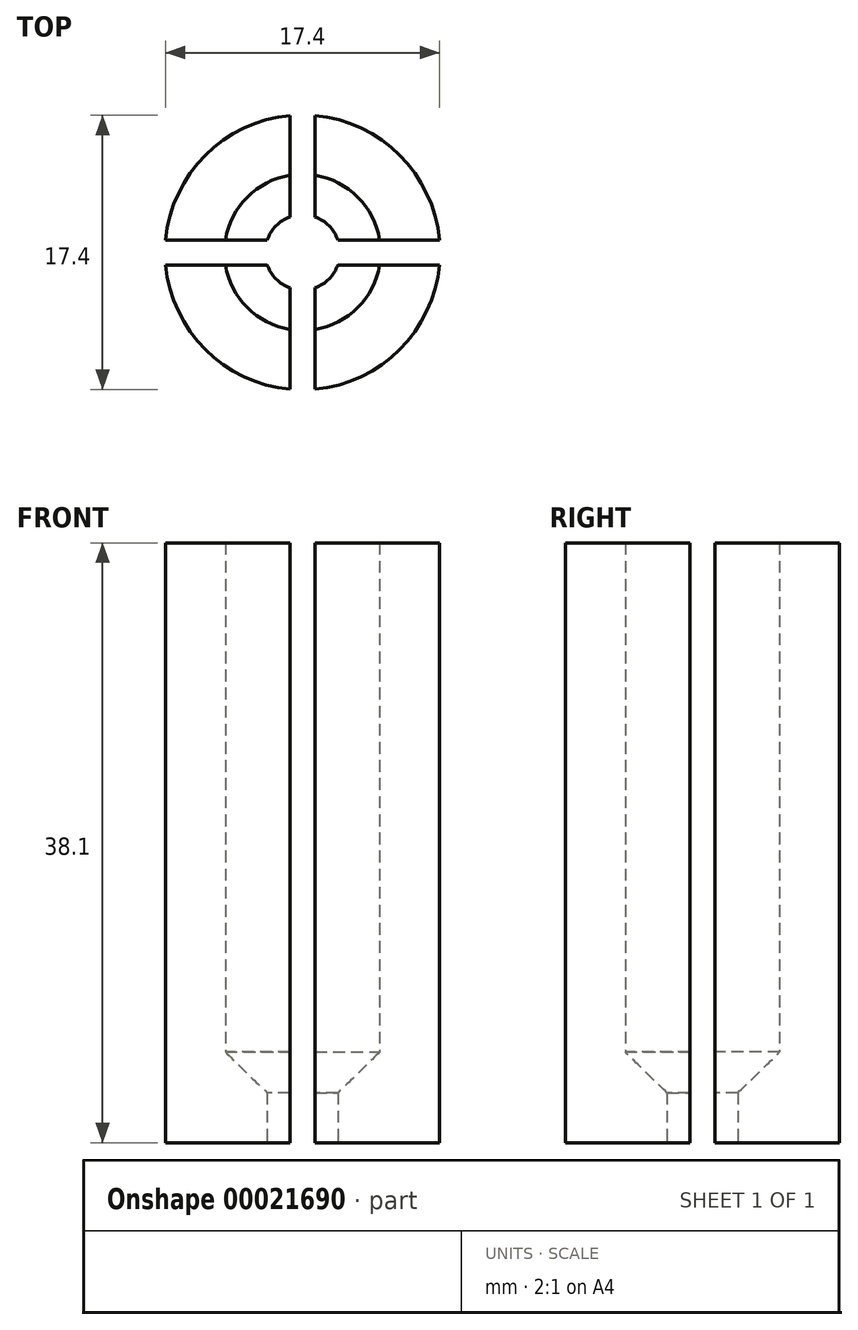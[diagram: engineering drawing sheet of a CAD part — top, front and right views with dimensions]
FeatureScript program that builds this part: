
annotation { "Feature Type Name" : "Feature", "Feature Type Description" : "" }
export const myFeature = defineFeature(function(context is Context, id is Id, definition is map)
    precondition{}
    {
        {
            var Q0;
            Q0=qCreatedBy(makeId("Front.planeOp"),FACE);
            var sketch = newSketch(context, id + "F0", { "sketchPlane" : qUnion([Q0])});
            skLineSegment(sketch, "E0", {"start": v(-16.12, 0) * mm, "end": v(18.02, 0) * mm, "construction": true});
            skLineSegment(sketch, "E1", {"start": v(-8.73, 0) * mm, "end": v(-2.38, 0) * mm});
            skLineSegment(sketch, "E2", {"start": v(-2.38, 0) * mm, "end": v(-2.38, 3.18) * mm});
            skLineSegment(sketch, "E3", {"start": v(-2.38, 3.18) * mm, "end": v(-4.96, 5.75) * mm});
            skLineSegment(sketch, "E4", {"start": v(-4.96, 5.75) * mm, "end": v(-4.96, 38.1) * mm});
            skLineSegment(sketch, "E5", {"start": v(-4.96, 38.1) * mm, "end": v(-8.73, 38.1) * mm});
            skLineSegment(sketch, "E6", {"start": v(-8.73, 38.1) * mm, "end": v(-8.73, 0) * mm});
            skLineSegment(sketch, "E7", {"start": v(0, -2.72) * mm, "end": v(0, 42.46) * mm, "construction": true});
            skSolve(sketch);
        }
        {
            var Q0;
            Q0=makeQuery(id+"F0.imprint","IMPRINT",FACE,{"disambiguationData":[TD([[makeQuery(id+"F0.imprint","IMPRINT",EDGE,{"derivedFrom":sQuery(id+"F0.wireOp",EDGE,"E1")}),1.0]])]});
            var Q1;
            Q1=sQuery(id+"F0.wireOp",EDGE,"E7");
            revolve(context, id + "F1", {"entities" : qUnion([Q0]), "axis" : qUnion([Q1]), "revolveType" : RevolveType.FULL});
        }
        {
            var Q0;
            Q0=makeQuery(id+"F1.opRevolve","SWEPT_FACE",FACE,{"disambiguationData":[OSD([sQuery(id+"F0.wireOp",EDGE,"E5")])]});
            var sketch = newSketch(context, id + "F2", { "sketchPlane" : qUnion([Q0])});
            skLineSegment(sketch, "E8", {"start": v(-0.8, 8.73) * mm, "end": v(0.8, 8.73) * mm});
            skLineSegment(sketch, "E9", {"start": v(0.8, 8.73) * mm, "end": v(0.8, 0.8) * mm});
            skLineSegment(sketch, "E10", {"start": v(0.8, 0.8) * mm, "end": v(8.73, 0.8) * mm});
            skLineSegment(sketch, "E11", {"start": v(8.73, 0.8) * mm, "end": v(8.73, -0.8) * mm});
            skLineSegment(sketch, "E12", {"start": v(8.73, -0.8) * mm, "end": v(0.8, -0.8) * mm});
            skLineSegment(sketch, "E13", {"start": v(0.8, -0.8) * mm, "end": v(0.8, -8.73) * mm});
            skLineSegment(sketch, "E14", {"start": v(0.8, -8.73) * mm, "end": v(-0.8, -8.73) * mm});
            skLineSegment(sketch, "E15", {"start": v(-0.8, -8.73) * mm, "end": v(-0.8, -0.8) * mm});
            skLineSegment(sketch, "E16", {"start": v(-0.8, -0.8) * mm, "end": v(-8.73, -0.8) * mm});
            skLineSegment(sketch, "E17", {"start": v(-8.73, -0.8) * mm, "end": v(-8.73, 0.8) * mm});
            skLineSegment(sketch, "E18", {"start": v(-8.73, 0.8) * mm, "end": v(-0.8, 0.8) * mm});
            skLineSegment(sketch, "E19", {"start": v(-0.8, 0.8) * mm, "end": v(-0.8, 8.73) * mm});
            skLineSegment(sketch, "E20", {"start": v(13.68, 0) * mm, "end": v(-10.76, 0) * mm, "construction": true});
            skLineSegment(sketch, "E21", {"start": v(0, -10.25) * mm, "end": v(0, 9.26) * mm, "construction": true});
            skSolve(sketch);
        }
        {
            var Q0;
            Q0 = qSketchRegion(id + "F2", true);
            extrude(context, id + "F3", {"entities" : qUnion([Q0]), "operationType" : NewBodyOperationType.REMOVE, "endBound" : BoundingType.THROUGH_ALL, "oppositeDirection" : true, "depth" : 25.4 * mm});
        }
    });
